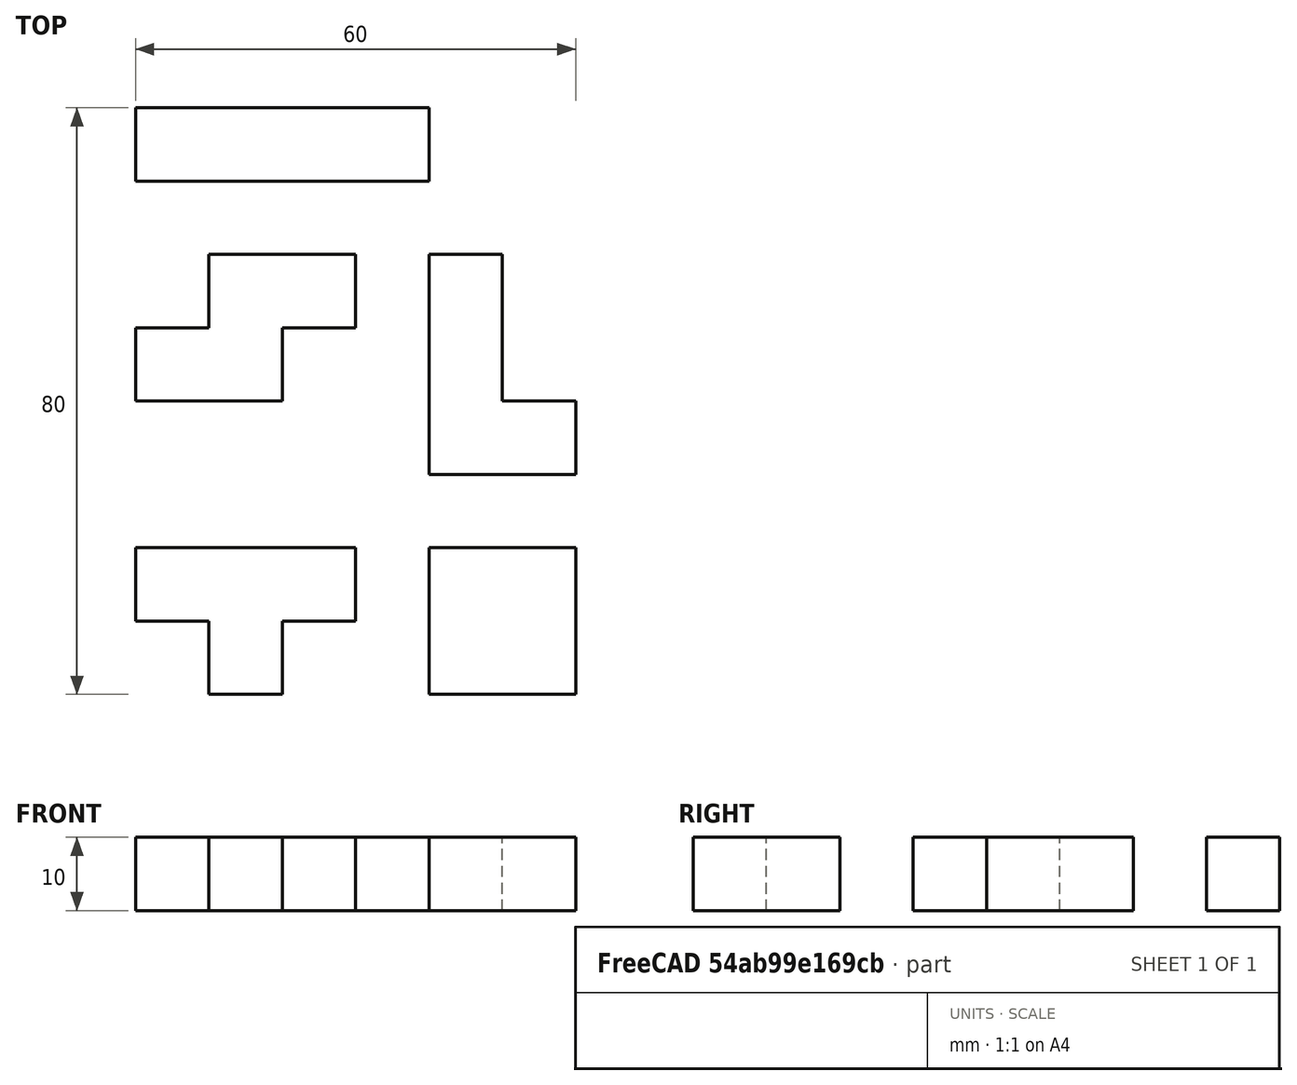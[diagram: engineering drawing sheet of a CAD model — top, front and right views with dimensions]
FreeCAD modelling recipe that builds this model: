
FCSTD DOCUMENT  (FreeCAD 1.0R39319 (Git))
Label: ojt1_t05r03_tetris
License: All rights reserved
LicenseURL: https://en.wikipedia.org/wiki/All_rights_reserved
objects: Part::Box×16, Part::MultiFuse×5
note: 21 computed .brp shape members not serialized (recipe doc carries the construction recipe); baked Part::Feature solids carry a one-line shape summary decoded from their .brp

FEATURE [Part::Box] Box  label="llarg"
  AttacherType = Attacher::AttachEngine3D
  Height = 10
  Length = 40
  Placement = pos=(0,40,0) rot=(0,0,1;0rad)
  Width = 10
FEATURE [Part::Box] Box001  label="Cub001"
  AttacherType = Attacher::AttachEngine3D
  Height = 10
  Length = 20
  Width = 10
FEATURE [Part::Box] Box002  label="Cub"
  AttacherType = Attacher::AttachEngine3D
  Height = 10
  Length = 10
  Placement = pos=(10,10,0) rot=(0,0,1;0rad)
  Width = 10
FEATURE [Part::MultiFuse] Fusion
  Refine = true
  Shapes = -> [Box001,Box002]
FEATURE [Part::Box] Box003  label="Cub002"
  AttacherType = Attacher::AttachEngine3D
  Height = 10
  Length = 10
  Placement = pos=(20,10,0) rot=(0,0,1;0rad)
  Width = 10
FEATURE [Part::MultiFuse] Fusion001  label="Z"
  Placement = pos=(0,10,0) rot=(0,0,1;0rad)
  Refine = true
  Shapes = -> [Fusion,Box003]
FEATURE [Part::Box] Box004  label="Cub003"
  AttacherType = Attacher::AttachEngine3D
  Height = 10
  Length = 10
  Placement = pos=(0,-20,0) rot=(0,0,1;0rad)
  Width = 10
FEATURE [Part::Box] Box005  label="Cub004"
  AttacherType = Attacher::AttachEngine3D
  Height = 10
  Length = 10
  Placement = pos=(10,-20,0) rot=(0,0,1;0rad)
  Width = 10
FEATURE [Part::Box] Box006  label="Cub005"
  AttacherType = Attacher::AttachEngine3D
  Height = 10
  Length = 10
  Placement = pos=(20,-20,0) rot=(0,0,1;0rad)
  Width = 10
FEATURE [Part::Box] Box007  label="Cub006"
  AttacherType = Attacher::AttachEngine3D
  Height = 10
  Length = 10
  Placement = pos=(10,-30,0) rot=(0,0,1;0rad)
  Width = 10
FEATURE [Part::MultiFuse] Fusion002
  Refine = true
  Shapes = -> [Box004,Box005,Box006,Box007]
FEATURE [Part::Box] Box008  label="Cub007"
  AttacherType = Attacher::AttachEngine3D
  Height = 10
  Length = 10
  Placement = pos=(40,20,0) rot=(0,0,1;0rad)
  Width = 10
FEATURE [Part::Box] Box009  label="Cub008"
  AttacherType = Attacher::AttachEngine3D
  Height = 10
  Length = 10
  Placement = pos=(40,10,0) rot=(0,0,1;0rad)
  Width = 10
FEATURE [Part::Box] Box010  label="Cub009"
  AttacherType = Attacher::AttachEngine3D
  Height = 10
  Length = 10
  Placement = pos=(40,0,0) rot=(0,0,1;0rad)
  Width = 10
FEATURE [Part::Box] Box011  label="Cub010"
  AttacherType = Attacher::AttachEngine3D
  Height = 10
  Length = 10
  Placement = pos=(50,0,0) rot=(0,0,1;0rad)
  Width = 10
FEATURE [Part::MultiFuse] Fusion003  label="L"
  Refine = true
  Shapes = -> [Box008,Box009,Box010,Box011]
FEATURE [Part::Box] Box012  label="Cub011"
  AttacherType = Attacher::AttachEngine3D
  Height = 10
  Length = 10
  Placement = pos=(50,-30,0) rot=(0,0,1;0rad)
  Width = 10
FEATURE [Part::Box] Box013  label="Cub012"
  AttacherType = Attacher::AttachEngine3D
  Height = 10
  Length = 10
  Placement = pos=(40,-30,0) rot=(0,0,1;0rad)
  Width = 10
FEATURE [Part::Box] Box014  label="Cub013"
  AttacherType = Attacher::AttachEngine3D
  Height = 10
  Length = 10
  Placement = pos=(40,-40,0) rot=(0,0,1;0rad)
  Width = 10
FEATURE [Part::Box] Box015  label="Cub014"
  AttacherType = Attacher::AttachEngine3D
  Height = 10
  Length = 10
  Placement = pos=(50,-40,0) rot=(0,0,1;0rad)
  Width = 10
FEATURE [Part::MultiFuse] Fusion004
  Placement = pos=(0,10,0) rot=(0,0,1;0rad)
  Refine = true
  Shapes = -> [Box012,Box013,Box014,Box015]
